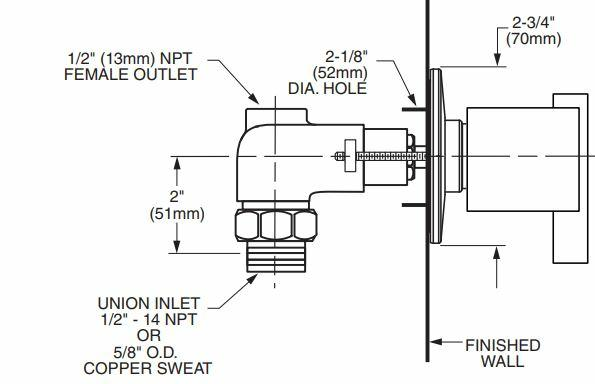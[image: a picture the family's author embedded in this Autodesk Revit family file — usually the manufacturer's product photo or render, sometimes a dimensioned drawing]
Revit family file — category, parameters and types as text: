
# Revit family: Diverter-American_Standard-Boulevard-T431.700_Series
name_source: partatom
category: Plumbing Fixtures
revit_build: Autodesk Revit 2015 (Build: 20140606_1530(x64)
units: mm (PartAtom-declared; Revit-internal decimal feet)

## types (2) — shared parameters
Assembly Code = D2020300
CW Connection = Yes
Cold Water Connection Diameter = 1/2"
Cold Water Connection Radius = 1/4"
Default Elevation = 48"
Description = Boulevard Diverter Valve Trim Kit
HW Connection = Yes
Height = 3"
Hot Water Connection Diameter = 1"
Hot Water Connection Radius = 1/4"
Installation Type = Wall Mounted
Length = 3 7/8"
Manufacturer = American Standard
Price = Prices may vary. Please consult Manufacturer Representative for most up-to-date price list.
Product Documentation Link = https://www.americanstandard.ca
Product Page URL = https://www.americanstandard.ca
Tempered Water Connection Diameter = 1/2"
Tempered Water Connection Radius = 1/4"
URL = https://americanstandard.ca
Width = 2 3/4"

## per-type parameters (varying)
| type | Finish | Material |
| T431.700.002 | Brass-American Standard-002-Chrome | Brass-American Standard-002-Chrome |
| T431.700.295 | Brass-American Standard-295-Brushed Nickel | Brass-American Standard-295-Brushed Nickel |

note: column(s) folded — value = type name in every type: Model

## geometry (parser evidence)
native form markers: Sweep x3
no freeform markers — native parametric forms only
